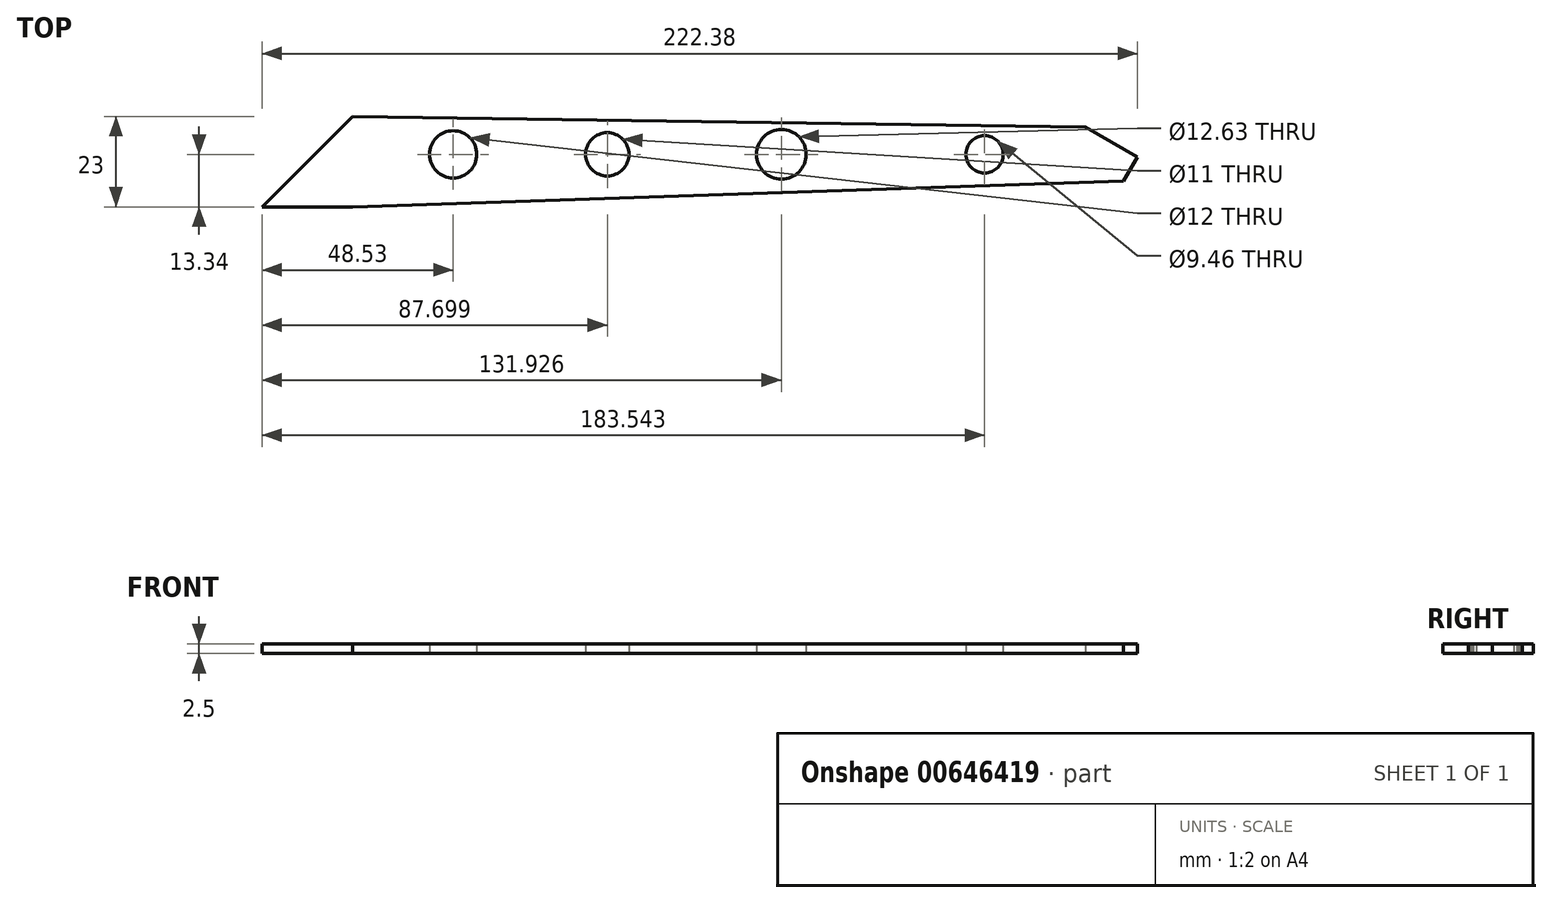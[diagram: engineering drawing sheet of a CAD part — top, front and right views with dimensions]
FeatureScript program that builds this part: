
annotation { "Feature Type Name" : "Feature", "Feature Type Description" : "" }
export const myFeature = defineFeature(function(context is Context, id is Id, definition is map)
    precondition{}
    {
        {
            var Q0;
            Q0=qCreatedBy(makeId("Top.planeOp"),FACE);
            var sketch = newSketch(context, id + "F0", { "sketchPlane" : qUnion([Q0])});
            skLineSegment(sketch, "E0", {"start": v(0, 0) * mm, "end": v(200, 0) * mm});
            skLineSegment(sketch, "E1", {"start": v(200, 0) * mm, "end": v(200, 6.67) * mm, "construction": true});
            skLineSegment(sketch, "E2", {"start": v(200, 6.67) * mm, "end": v(200, -6.67) * mm, "construction": true});
            skLineSegment(sketch, "E3", {"start": v(0, 9.66) * mm, "end": v(200, 6.67) * mm});
            skLineSegment(sketch, "E4", {"start": v(200, -6.67) * mm, "end": v(0, -13.34) * mm});
            skLineSegment(sketch, "E5", {"start": v(0, 9.66) * mm, "end": v(0, -13.34) * mm});
            skLineSegment(sketch, "E6", {"start": v(200, 6.67) * mm, "end": v(200, -6.67) * mm});
            skCircle(sketch, "E7", {"center": v(25.53, 0) * mm, "radius": 6 * mm});
            skCircle(sketch, "E8", {"center": v(108.93, 0) * mm, "radius": 6.31 * mm});
            skCircle(sketch, "E9", {"center": v(64.7, 0) * mm, "radius": 5.5 * mm});
            skCircle(sketch, "E10", {"center": v(160.54, 0) * mm, "radius": 4.73 * mm});
            skSolve(sketch);
        }
        {
            var Q0;
            Q0 = qSketchRegion(id + "F0", true);
            extrude(context, id + "F1", {"entities" : qUnion([Q0]), "depth" : 2.5 * mm, "offsetDistance" : 25 * mm});
        }
        {
            var Q0;
            Q0=makeQuery(id+"F1.opExtrude","CAP_FACE",FACE,{"disambiguationData":[OSD([sQuery(id+"F0.wireOp",EDGE,"E3"),sQuery(id+"F0.wireOp",EDGE,"E4"),sQuery(id+"F0.wireOp",EDGE,"E5"),sQuery(id+"F0.wireOp",EDGE,"E6"),sQuery(id+"F0.wireOp",EDGE,"E7"),sQuery(id+"F0.wireOp",EDGE,"E8"),sQuery(id+"F0.wireOp",EDGE,"E9"),sQuery(id+"F0.wireOp",EDGE,"E10")])],"isStart":false});
            var sketch = newSketch(context, id + "F2", { "sketchPlane" : qUnion([Q0])});
            skLineSegment(sketch, "E11", {"start": v(200, 0) * mm, "end": v(0, 0) * mm, "construction": true});
            skLineSegment(sketch, "E12", {"start": v(200, -6.67) * mm, "end": v(200, 0.33) * mm, "construction": true});
            skLineSegment(sketch, "E13", {"start": v(200, 0.33) * mm, "end": v(188.74, 6.84) * mm});
            skSolve(sketch);
        }
        {
            var Q0;
            {var subQ0=sQuery(id+"F2.wireOp",EDGE,"E13");Q0=makeQuery(id+"F2.imprint","IMPRINT",FACE,{"disambiguationData":[TD([[makeQuery(id+"F2.imprint","IMPRINT",EDGE,{"derivedFrom":subQ0}),-1.0]])]});}
            extrude(context, id + "F3", {"entities" : qUnion([Q0]), "operationType" : NewBodyOperationType.REMOVE, "oppositeDirection" : true, "depth" : 25 * mm, "offsetDistance" : 25 * mm});
        }
        {
            var Q0;
            Q0=makeQuery(id+"F1.opExtrude","CAP_FACE",FACE,{"disambiguationData":[OSD([sQuery(id+"F0.wireOp",EDGE,"E3"),sQuery(id+"F0.wireOp",EDGE,"E4"),sQuery(id+"F0.wireOp",EDGE,"E5"),sQuery(id+"F0.wireOp",EDGE,"E6"),sQuery(id+"F0.wireOp",EDGE,"E7"),sQuery(id+"F0.wireOp",EDGE,"E8"),sQuery(id+"F0.wireOp",EDGE,"E9"),sQuery(id+"F0.wireOp",EDGE,"E10")])],"isStart":true});
            var sketch = newSketch(context, id + "F4", { "sketchPlane" : qUnion([Q0])});
            skLineSegment(sketch, "E14", {"start": v(200, -0.33) * mm, "end": v(195.88, 6.8) * mm});
            skSolve(sketch);
        }
        {
            var Q0;
            {var subQ0=sQuery(id+"F4.wireOp",EDGE,"E14");Q0=makeQuery(id+"F4.imprint","IMPRINT",FACE,{"disambiguationData":[TD([[makeQuery(id+"F4.imprint","IMPRINT",EDGE,{"derivedFrom":subQ0}),-1.0]])]});}
            extrude(context, id + "F5", {"entities" : qUnion([Q0]), "operationType" : NewBodyOperationType.REMOVE, "oppositeDirection" : true, "depth" : 25 * mm, "offsetDistance" : 25 * mm});
        }
        {
            var Q0;
            Q0=makeQuery(id+"F1.opExtrude","CAP_FACE",FACE,{"disambiguationData":[OSD([sQuery(id+"F0.wireOp",EDGE,"E3"),sQuery(id+"F0.wireOp",EDGE,"E4"),sQuery(id+"F0.wireOp",EDGE,"E5"),sQuery(id+"F0.wireOp",EDGE,"E6"),sQuery(id+"F0.wireOp",EDGE,"E7"),sQuery(id+"F0.wireOp",EDGE,"E8"),sQuery(id+"F0.wireOp",EDGE,"E9"),sQuery(id+"F0.wireOp",EDGE,"E10")])],"isStart":true});
            var sketch = newSketch(context, id + "F6", { "sketchPlane" : qUnion([Q0])});
            skLineSegment(sketch, "E15", {"start": v(195.88, 6.8) * mm, "end": v(199.38, 0.74) * mm});
            skLineSegment(sketch, "E16", {"start": v(199.38, 0.74) * mm, "end": v(186.19, -6.87) * mm});
            skSolve(sketch);
        }
        {
            var Q0;
            {var subQ0=sQuery(id+"F6.wireOp",EDGE,"E16");Q0=makeQuery(id+"F6.imprint","IMPRINT",FACE,{"disambiguationData":[TD([[makeQuery(id+"F6.imprint","IMPRINT",EDGE,{"derivedFrom":subQ0}),1.0]])]});}
            extrude(context, id + "F7", {"entities" : qUnion([Q0]), "operationType" : NewBodyOperationType.REMOVE, "oppositeDirection" : true, "depth" : 25 * mm, "offsetDistance" : 25 * mm});
        }
        {
            var Q0;
            Q0=makeQuery(id+"F1.opExtrude","CAP_FACE",FACE,{"disambiguationData":[OSD([sQuery(id+"F0.wireOp",EDGE,"E3"),sQuery(id+"F0.wireOp",EDGE,"E4"),sQuery(id+"F0.wireOp",EDGE,"E5"),sQuery(id+"F0.wireOp",EDGE,"E6"),sQuery(id+"F0.wireOp",EDGE,"E7"),sQuery(id+"F0.wireOp",EDGE,"E8"),sQuery(id+"F0.wireOp",EDGE,"E9"),sQuery(id+"F0.wireOp",EDGE,"E10")])],"isStart":true});
            var sketch = newSketch(context, id + "F8", { "sketchPlane" : qUnion([Q0])});
            skLineSegment(sketch, "E17", {"start": v(0, 13.34) * mm, "end": v(-23, 13.34) * mm});
            skLineSegment(sketch, "E18", {"start": v(0, -9.66) * mm, "end": v(-23, 13.34) * mm});
            skSolve(sketch);
        }
        {
            var Q0;
            Q0=makeQuery(id+"F8.imprint","IMPRINT",FACE,{"disambiguationData":[TD([[makeQuery(id+"F8.imprint","IMPRINT",EDGE,{"derivedFrom":sQuery(id+"F8.wireOp",EDGE,"E17")}),1.0]])]});
            extrude(context, id + "F9", {"entities" : qUnion([Q0]), "operationType" : NewBodyOperationType.ADD, "oppositeDirection" : true, "depth" : 2.5 * mm, "offsetDistance" : 25 * mm});
        }
    });
